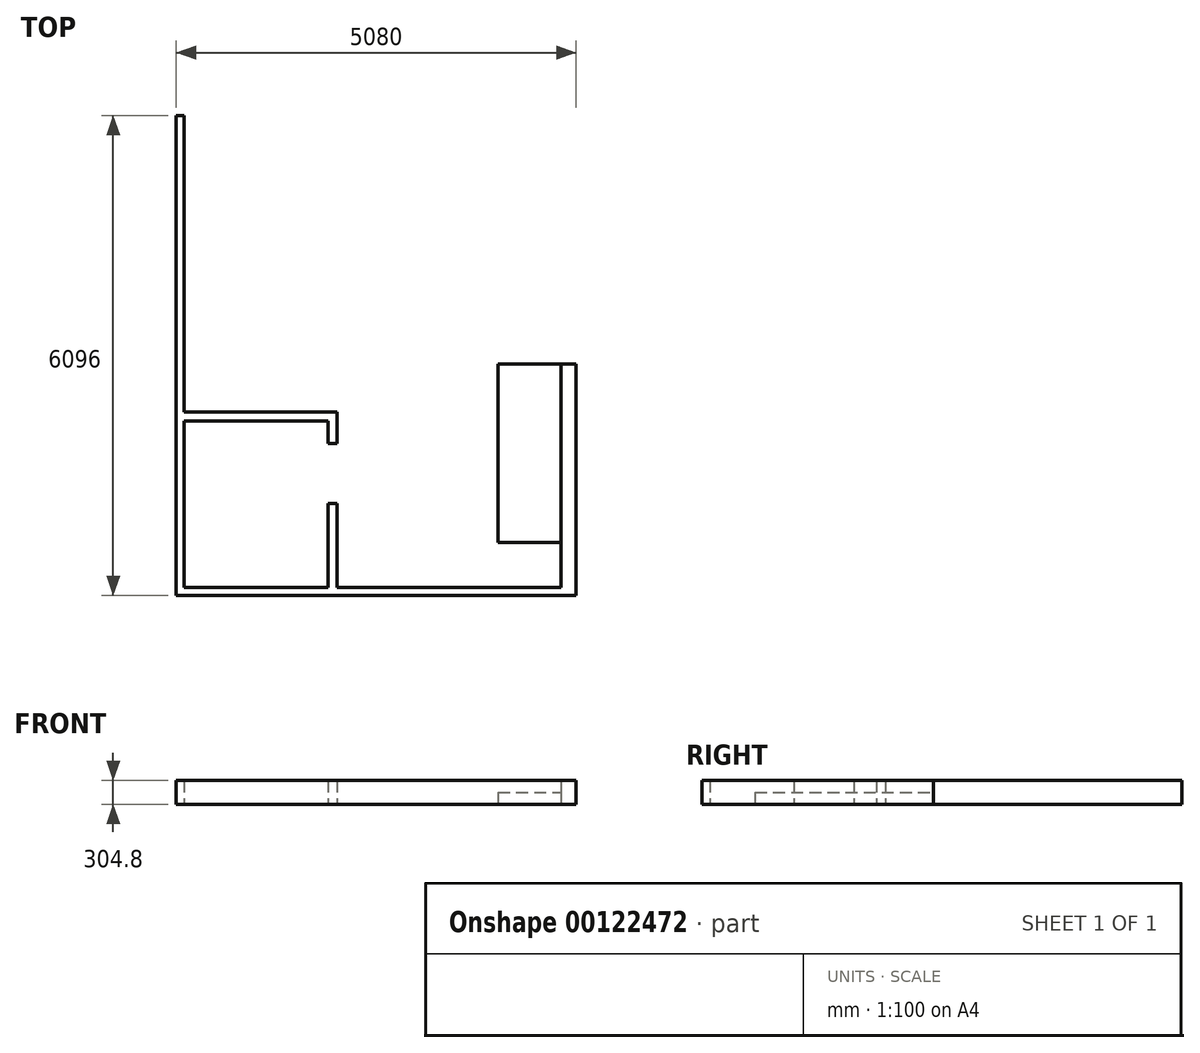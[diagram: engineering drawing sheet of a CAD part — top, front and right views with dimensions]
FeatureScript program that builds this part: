
annotation { "Feature Type Name" : "Feature", "Feature Type Description" : "" }
export const myFeature = defineFeature(function(context is Context, id is Id, definition is map)
    precondition{}
    {
        {
            var Q0;
            Q0=qCreatedBy(makeId("Top.planeOp"),FACE);
            var sketch = newSketch(context, id + "F0", { "sketchPlane" : qUnion([Q0])});
            skLineSegment(sketch, "E0.bottom", {"start": v(0, 0) * mm, "end": v(5080, 0) * mm});
            skLineSegment(sketch, "E0.top", {"start": v(0, 6096) * mm, "end": v(5080, 6096) * mm});
            skLineSegment(sketch, "E0.left", {"start": v(0, 0) * mm, "end": v(0, 6096) * mm});
            skLineSegment(sketch, "E0.right", {"start": v(5080, 0) * mm, "end": v(5080, 6096) * mm});
            skLineSegment(sketch, "E1.bottom", {"start": v(2203.45, 2959.1) * mm, "end": v(2343.15, 2959.1) * mm});
            skLineSegment(sketch, "E1.top", {"start": v(2203.45, 3098.8) * mm, "end": v(2343.15, 3098.8) * mm});
            skLineSegment(sketch, "E1.left", {"start": v(2203.45, 2959.1) * mm, "end": v(2203.45, 3098.8) * mm});
            skLineSegment(sketch, "E1.right", {"start": v(2343.15, 2959.1) * mm, "end": v(2343.15, 3098.8) * mm});
            skLineSegment(sketch, "E2.bottom", {"start": v(3378.2, 2959.1) * mm, "end": v(3517.9, 2959.1) * mm});
            skLineSegment(sketch, "E2.top", {"start": v(3378.2, 3098.8) * mm, "end": v(3517.9, 3098.8) * mm});
            skLineSegment(sketch, "E2.left", {"start": v(3378.2, 2959.1) * mm, "end": v(3378.2, 3098.8) * mm});
            skLineSegment(sketch, "E2.right", {"start": v(3517.9, 2959.1) * mm, "end": v(3517.9, 3098.8) * mm});
            skSolve(sketch);
        }
        {
            var Q0;
            Q0=qCreatedBy(makeId("Top.planeOp"),FACE);
            var sketch = newSketch(context, id + "F1", { "sketchPlane" : qUnion([Q0])});
            skLineSegment(sketch, "E3", {"start": v(0, 3028.95) * mm, "end": v(5080, 3028.95) * mm, "construction": true});
            skLineSegment(sketch, "E4.bottom", {"start": v(0, 3119.12) * mm, "end": v(5080, 3119.12) * mm});
            skLineSegment(sketch, "E4.top", {"start": v(0, 2938.78) * mm, "end": v(5080, 2938.78) * mm});
            skLineSegment(sketch, "E4.left", {"start": v(0, 3119.12) * mm, "end": v(0, 2938.78) * mm});
            skLineSegment(sketch, "E4.right", {"start": v(5080, 3119.12) * mm, "end": v(5080, 2938.78) * mm});
            skSolve(sketch);
        }
        {
            var Q0;
            Q0=qCreatedBy(makeId("Top.planeOp"),FACE);
            var sketch = newSketch(context, id + "F2", { "sketchPlane" : qUnion([Q0])});
            skLineSegment(sketch, "E5.bottom", {"start": v(4089.4, 2938.78) * mm, "end": v(5080, 2938.78) * mm});
            skLineSegment(sketch, "E5.top", {"start": v(4089.4, 673.1) * mm, "end": v(5080, 673.1) * mm});
            skLineSegment(sketch, "E5.left", {"start": v(4089.4, 2938.78) * mm, "end": v(4089.4, 673.1) * mm});
            skLineSegment(sketch, "E5.right", {"start": v(5080, 2938.78) * mm, "end": v(5080, 673.1) * mm});
            skLineSegment(sketch, "E6", {"start": v(5080, 2938.78) * mm, "end": v(4089.4, 673.1) * mm, "construction": true});
            skLineSegment(sketch, "E7", {"start": v(4089.4, 2938.78) * mm, "end": v(5080, 673.1) * mm, "construction": true});
            skSolve(sketch);
        }
        {
            var Q0;
            Q0=qCreatedBy(makeId("Top.planeOp"),FACE);
            var sketch = newSketch(context, id + "F3", { "sketchPlane" : qUnion([Q0])});
            skLineSegment(sketch, "E8", {"start": v(101.6, 6096) * mm, "end": v(101.6, 101.6) * mm});
            skLineSegment(sketch, "E9", {"start": v(101.6, 101.6) * mm, "end": v(4889.5, 101.6) * mm});
            skLineSegment(sketch, "E10", {"start": v(4889.5, 101.6) * mm, "end": v(4889.5, 2938.78) * mm});
            skLineSegment(sketch, "E11", {"start": v(101.6, 6096) * mm, "end": v(0, 6096) * mm});
            skLineSegment(sketch, "E12", {"start": v(0, 6096) * mm, "end": v(0, 0) * mm});
            skLineSegment(sketch, "E13", {"start": v(0, 0) * mm, "end": v(5080, 0) * mm});
            skLineSegment(sketch, "E14", {"start": v(5080, 0) * mm, "end": v(5080, 2938.78) * mm});
            skLineSegment(sketch, "E15", {"start": v(5080, 2938.78) * mm, "end": v(4889.5, 2938.78) * mm});
            skSolve(sketch);
        }
        {
            var Q0;
            Q0 = qSketchRegion(id + "F3", true);
            extrude(context, id + "F4", {"entities" : qUnion([Q0]), "depth" : 304.8 * mm, "offsetDistance" : 25.4 * mm});
        }
        {
            var Q0;
            Q0=makeQuery(id+"F2.imprint","IMPRINT",FACE,{"disambiguationData":[TD([[makeQuery(id+"F2.imprint","IMPRINT",EDGE,{"derivedFrom":sQuery(id+"F2.wireOp",EDGE,"E5.bottom")}),-1.0]])]});
            extrude(context, id + "F5", {"entities" : qUnion([Q0]), "operationType" : NewBodyOperationType.ADD, "depth" : 152.4 * mm, "offsetDistance" : 25.4 * mm});
        }
        {
            var Q0;
            Q0=qCreatedBy(makeId("Top.planeOp"),FACE);
            var sketch = newSketch(context, id + "F6", { "sketchPlane" : qUnion([Q0])});
            skLineSegment(sketch, "E16", {"start": v(101.6, 2329.18) * mm, "end": v(2044.7, 2329.18) * mm});
            skLineSegment(sketch, "E17", {"start": v(2044.7, 2329.18) * mm, "end": v(2044.7, 1930.4) * mm});
            skLineSegment(sketch, "E18", {"start": v(2044.7, 1930.4) * mm, "end": v(1930.4, 1930.4) * mm});
            skLineSegment(sketch, "E19", {"start": v(1930.4, 1930.4) * mm, "end": v(1930.4, 2214.88) * mm});
            skLineSegment(sketch, "E20", {"start": v(1930.4, 2214.88) * mm, "end": v(101.6, 2214.88) * mm});
            skLineSegment(sketch, "E21", {"start": v(101.6, 2214.88) * mm, "end": v(101.6, 2329.18) * mm});
            skLineSegment(sketch, "E22", {"start": v(1930.4, 1168.4) * mm, "end": v(1930.4, 101.6) * mm});
            skLineSegment(sketch, "E23", {"start": v(1930.4, 101.6) * mm, "end": v(2044.7, 101.6) * mm});
            skLineSegment(sketch, "E24", {"start": v(2044.7, 101.6) * mm, "end": v(2044.7, 1168.4) * mm});
            skLineSegment(sketch, "E25", {"start": v(2044.7, 1168.4) * mm, "end": v(1930.4, 1168.4) * mm});
            skSolve(sketch);
        }
        {
            var Q0;
            Q0 = qSketchRegion(id + "F6", true);
            extrude(context, id + "F7", {"entities" : qUnion([Q0]), "operationType" : NewBodyOperationType.ADD, "depth" : 304.8 * mm, "offsetDistance" : 25.4 * mm});
        }
    });
